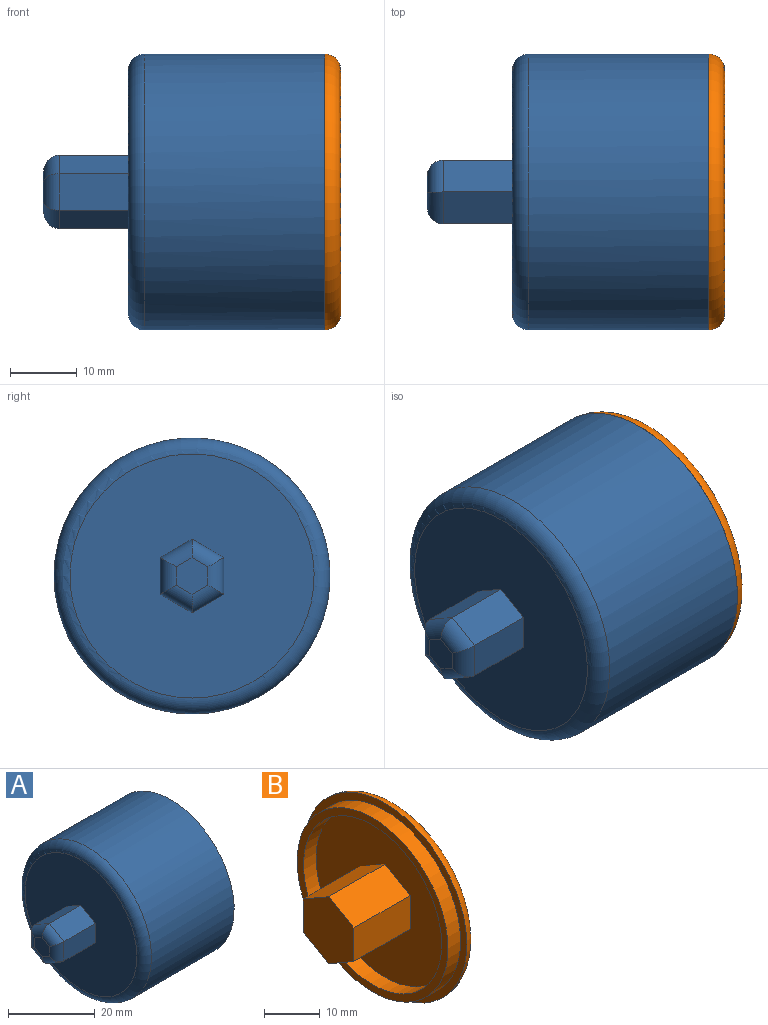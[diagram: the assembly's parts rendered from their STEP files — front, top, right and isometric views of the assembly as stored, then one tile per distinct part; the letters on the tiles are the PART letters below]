
ASSEMBLY  parts=2 mates=1
PART A: 27 faces, bbox 42.1x44.7x44.7 mm
  f0: plane 10.32x4.76mm, normal (0,0.5,0.87), area 56.7mm2, adj f1,f5,f9,f22
  f1: plane 10.32x4.76mm, normal (0,-0.5,0.87), area 56.7mm2, adj f0,f2,f9,f21
  f2: plane 10.32x5.5mm, normal (0,-1,0), area 56.7mm2, adj f1,f3,f9,f23
  f3: plane 10.32x4.76mm, normal (0,-0.5,-0.87), area 56.7mm2, adj f2,f4,f9,f25
  f4: plane 10.32x4.76mm, normal (0,0.5,-0.87), area 56.7mm2, adj f3,f5,f9,f26
  f5: plane 10.32x5.5mm, normal (0,1,0), area 56.7mm2, adj f0,f4,f9,f24
  f6: plane 5.5x4.76mm, normal (-1,0,0), area 19.6mm2, adj f21,f22,f23,f24,f25,f26
  f7: cylinder r=20.64mm len=41.28mm, axis (-1,0,0), area 3498.6mm2, adj f8,f20
  f8: plane 41.28x41.28mm, normal (1,0,0), area 197.9mm2, adj f7,f17
  f9: plane 36.51x36.51mm, normal (-1,0,0), area 968.5mm2, adj f0,f1,f2,f3,f4,f5,f20
  f10: plane 12.7x3.18mm, normal (0,-0.5,-0.87), area 46.6mm2, adj f11,f15,f16,f18
  f11: plane 12.7x3.18mm, normal (0,0.5,-0.87), area 46.6mm2, adj f10,f12,f16,f18
  f12: plane 12.7x3.67mm, normal (0,1,0), area 46.6mm2, adj f11,f13,f16,f18
  f13: plane 12.7x3.18mm, normal (0,0.5,0.87), area 46.6mm2, adj f12,f14,f16,f18
  f14: plane 12.7x3.18mm, normal (0,-0.5,0.87), area 46.6mm2, adj f13,f15,f16,f18
  f15: plane 12.7x3.67mm, normal (0,-1,0), area 46.6mm2, adj f10,f14,f16,f18
  f16: plane 7.33x6.35mm, normal (1,0,0), area 34.9mm2, adj f10,f11,f12,f13,f14,f15
  f17: cylinder r=19.05mm len=38.1mm, axis (-1,0,0), area 3229.5mm2, adj f8,f19
  f18: plane 36.51x36.51mm, normal (1,0,0), area 1012.1mm2, adj f10,f11,f12,f13,f14,f15,f19
  f19: torus R=18.26mm, axis (1,0,0), area 147mm2, adj f17,f18
  f20: torus R=18.26mm, axis (1,0,0), area 464.7mm2, adj f7,f9
  f21: cylinder r=2.38mm len=5.95mm, axis (0,-0.87,-0.5), area 16.8mm2, adj f1,f6,f22,f23
  f22: cylinder r=2.38mm len=5.95mm, axis (0,-0.87,0.5), area 16.8mm2, adj f0,f6,f21,f24
  f23: cylinder r=2.38mm len=5.5mm, axis (0,0,-1), area 16.8mm2, adj f2,f6,f21,f25
  f24: cylinder r=2.38mm len=5.5mm, axis (0,0,1), area 16.8mm2, adj f5,f6,f22,f26
  f25: cylinder r=2.38mm len=5.95mm, axis (0,0.87,-0.5), area 16.8mm2, adj f3,f6,f23,f26
  f26: cylinder r=2.38mm len=5.95mm, axis (0,0.87,0.5), area 16.8mm2, adj f4,f6,f24,f25
PART B: 21 faces, bbox 16.7x44.7x44.7 mm
  f0: plane 36.51x36.51mm, normal (1,0,0), area 967.7mm2, adj f2,f3,f4,f5,f6,f7,f20
  f1: plane 41.28x41.28mm, normal (-1,0,0), area 197.9mm2, adj f10,f20
  f2: plane 9.53x4.79mm, normal (0,-0.5,-0.87), area 52.7mm2, adj f0,f3,f7,f8
  f3: plane 9.53x4.79mm, normal (0,0.5,-0.87), area 52.7mm2, adj f0,f2,f4,f8
  f4: plane 9.53x5.53mm, normal (0,1,0), area 52.7mm2, adj f0,f3,f5,f8
  f5: plane 9.53x4.79mm, normal (0,0.5,0.87), area 52.7mm2, adj f0,f4,f6,f8
  f6: plane 9.53x4.79mm, normal (0,-0.5,0.87), area 52.7mm2, adj f0,f5,f7,f8
  f7: plane 9.53x5.53mm, normal (0,-1,0), area 52.7mm2, adj f0,f2,f6,f8
  f8: plane 11.06x9.58mm, normal (1,0,0), area 79.4mm2, adj f2,f3,f4,f5,f6,f7
  f9: cylinder r=17.46mm len=34.93mm, axis (1,0,0), area 348.4mm2, adj f11,f19
  f10: cylinder r=19.05mm len=38.1mm, axis (1,0,0), area 380mm2, adj f1,f11
  f11: plane 38.1x38.1mm, normal (-1,0,0), area 182.1mm2, adj f9,f10
  f12: plane 14.66x12.7mm, normal (-1,0,0), area 139.7mm2, adj f13,f14,f15,f16,f17,f18
  f13: plane 14.29x7.33mm, normal (0,1,0), area 104.8mm2, adj f12,f14,f18,f19
  f14: plane 14.29x6.35mm, normal (0,0.5,-0.87), area 104.8mm2, adj f12,f13,f15,f19
  f15: plane 14.29x6.35mm, normal (0,-0.5,-0.87), area 104.8mm2, adj f12,f14,f16,f19
  f16: plane 14.29x7.33mm, normal (0,-1,0), area 104.8mm2, adj f12,f15,f17,f19
  f17: plane 14.29x6.35mm, normal (0,-0.5,0.87), area 104.8mm2, adj f12,f16,f18,f19
  f18: plane 14.29x6.35mm, normal (0,0.5,0.87), area 104.8mm2, adj f12,f13,f17,f19
  f19: plane 34.93x34.93mm, normal (-1,0,0), area 818.3mm2, adj f9,f13,f14,f15,f16,f17,f18
  f20: torus R=18.26mm, axis (1,0,0), area 464.7mm2, adj f0,f1
PLACE A at identity
PLACE B t=(42.06,0,0)mm
MATE fastened A.f7 <-> B.f9  axis (1,0,0) through (42.06,0,0)mm
